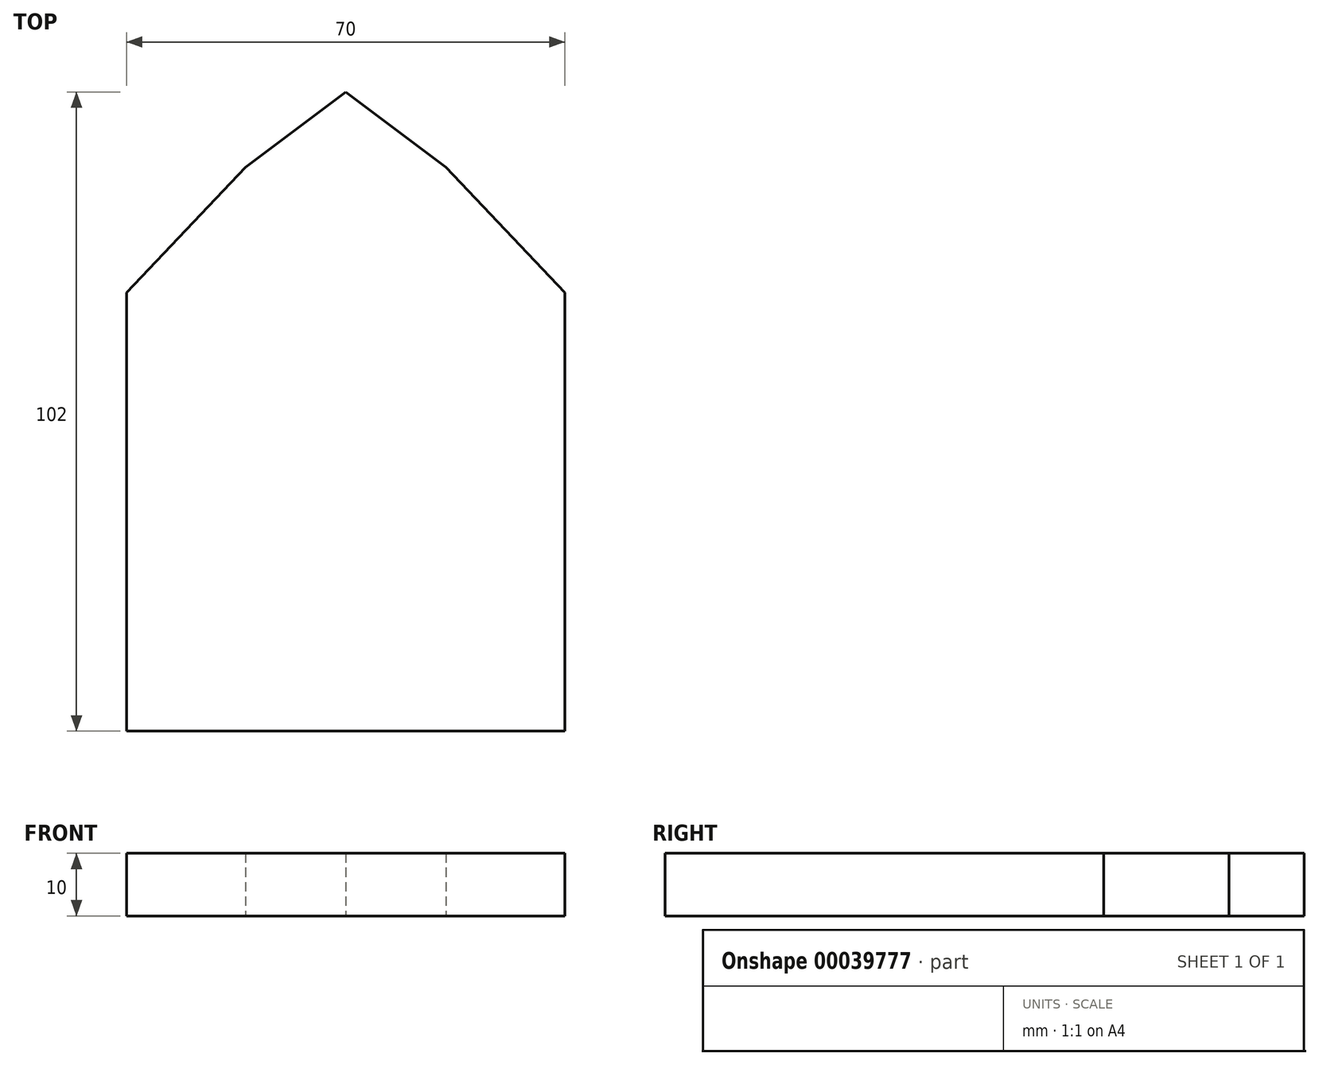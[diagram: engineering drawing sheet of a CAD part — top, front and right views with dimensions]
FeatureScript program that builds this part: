
annotation { "Feature Type Name" : "Feature", "Feature Type Description" : "" }
export const myFeature = defineFeature(function(context is Context, id is Id, definition is map)
    precondition{}
    {
        {
            var Q0;
            Q0=qCreatedBy(makeId("Top.planeOp"),FACE);
            var sketch = newSketch(context, id + "F0", { "sketchPlane" : qUnion([Q0])});
            skPoint(sketch, "E0.rect.middle", {"position": v(-37.62, -35.29) * mm});
            skLineSegment(sketch, "E1.rect.bottom", {"start": v(-2.4, -35) * mm, "end": v(-72.4, -35) * mm});
            skLineSegment(sketch, "E1.rect.top", {"start": v(-2.4, 35) * mm, "end": v(-72.4, 35) * mm});
            skLineSegment(sketch, "E1.rect.left", {"start": v(-2.4, -35) * mm, "end": v(-2.4, 35) * mm});
            skLineSegment(sketch, "E1.rect.right", {"start": v(-72.4, -35) * mm, "end": v(-72.4, 35) * mm});
            skPoint(sketch, "E1.rect.middle", {"position": v(-37.4, 0) * mm});
            skLineSegment(sketch, "E2", {"start": v(-72.4, 35) * mm, "end": v(-53.4, 55) * mm});
            skLineSegment(sketch, "E3", {"start": v(-53.4, 55) * mm, "end": v(-21.4, 55) * mm});
            skLineSegment(sketch, "E4", {"start": v(-21.4, 55) * mm, "end": v(-2.4, 35) * mm});
            skLineSegment(sketch, "E5", {"start": v(-53.4, 55) * mm, "end": v(-37.4, 67) * mm});
            skLineSegment(sketch, "E6", {"start": v(-37.4, 67) * mm, "end": v(-21.4, 55) * mm});
            skLineSegment(sketch, "E7", {"start": v(-41.5, 35) * mm, "end": v(-41.5, 55) * mm, "construction": true});
            skSolve(sketch);
        }
        {
            var Q0;
            Q0 = qSketchRegion(id + "F0", true);
            extrude(context, id + "F1", {"entities" : qUnion([Q0]), "depth" : 10 * mm});
        }
    });
